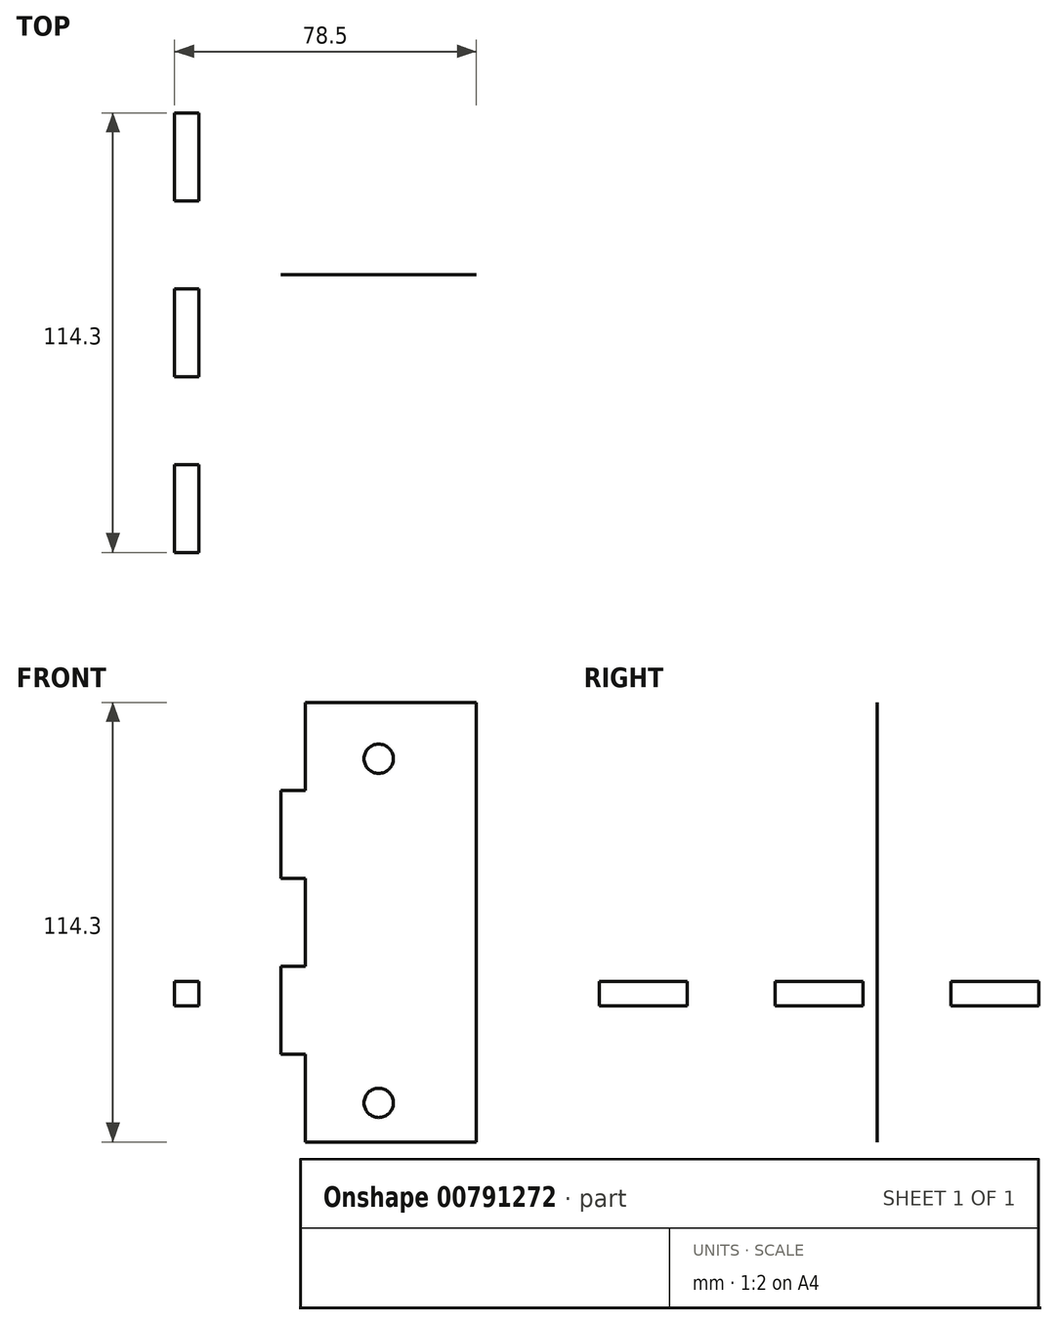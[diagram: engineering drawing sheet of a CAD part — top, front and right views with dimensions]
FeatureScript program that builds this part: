
annotation { "Feature Type Name" : "Feature", "Feature Type Description" : "" }
export const myFeature = defineFeature(function(context is Context, id is Id, definition is map)
    precondition{}
    {
        {
            var Q0;
            Q0=qCreatedBy(makeId("Top.planeOp"),FACE);
            var sketch = newSketch(context, id + "F0", { "sketchPlane" : qUnion([Q0])});
            skLineSegment(sketch, "E0.bottom", {"start": v(-68.61, 42.12) * mm, "end": v(-17.81, 42.12) * mm});
            skLineSegment(sketch, "E0.top", {"start": v(-68.61, -72.18) * mm, "end": v(-17.81, -72.18) * mm});
            skLineSegment(sketch, "E0.right", {"start": v(-17.81, 42.12) * mm, "end": v(-17.81, 19.26) * mm});
            skLineSegment(sketch, "E1", {"start": v(-17.81, -3.6) * mm, "end": v(-17.81, -26.46) * mm});
            skLineSegment(sketch, "E2", {"start": v(-17.81, -49.32) * mm, "end": v(-17.81, -72.18) * mm});
            skLineSegment(sketch, "E3", {"start": v(-17.81, -49.32) * mm, "end": v(-24.16, -49.32) * mm});
            skLineSegment(sketch, "E4", {"start": v(-24.16, -49.32) * mm, "end": v(-24.16, -26.46) * mm});
            skLineSegment(sketch, "E5", {"start": v(-24.16, -26.46) * mm, "end": v(-17.81, -26.46) * mm});
            skLineSegment(sketch, "E6", {"start": v(-17.81, -3.6) * mm, "end": v(-24.16, -3.6) * mm});
            skLineSegment(sketch, "E7", {"start": v(-24.16, -3.6) * mm, "end": v(-24.16, 19.26) * mm});
            skLineSegment(sketch, "E8", {"start": v(-24.16, 19.26) * mm, "end": v(-17.81, 19.26) * mm});
            skLineSegment(sketch, "E9.MirrorCS", {"start": v(-119.41, -49.32) * mm, "end": v(-113.06, -49.32) * mm});
            skLineSegment(sketch, "E10.MirrorCS", {"start": v(-113.06, 19.26) * mm, "end": v(-119.41, 19.26) * mm});
            skLineSegment(sketch, "E11.MirrorCS", {"start": v(-113.06, -26.46) * mm, "end": v(-119.41, -26.46) * mm});
            skLineSegment(sketch, "E12.MirrorCS", {"start": v(-119.41, -3.6) * mm, "end": v(-113.06, -3.6) * mm});
            skLineSegment(sketch, "E13.MirrorCS", {"start": v(-119.41, -49.32) * mm, "end": v(-119.41, -72.18) * mm});
            skLineSegment(sketch, "E14.MirrorCS", {"start": v(-119.41, -3.6) * mm, "end": v(-119.41, -26.46) * mm});
            skLineSegment(sketch, "E15.MirrorCS", {"start": v(-68.61, -72.18) * mm, "end": v(-119.41, -72.18) * mm});
            skLineSegment(sketch, "E16.MirrorCS", {"start": v(-113.06, -49.32) * mm, "end": v(-113.06, -26.46) * mm});
            skLineSegment(sketch, "E17.MirrorCS", {"start": v(-68.61, 42.12) * mm, "end": v(-119.41, 42.12) * mm});
            skLineSegment(sketch, "E18.MirrorCS", {"start": v(-113.06, -3.6) * mm, "end": v(-113.06, 19.26) * mm});
            skLineSegment(sketch, "E19.MirrorCS", {"start": v(-119.41, 42.12) * mm, "end": v(-119.41, 19.26) * mm});
            skLineSegment(sketch, "E20", {"start": v(-24.16, 19.26) * mm, "end": v(-24.16, 42.12) * mm});
            skLineSegment(sketch, "E21", {"start": v(-24.16, -49.32) * mm, "end": v(-24.16, -72.18) * mm});
            skLineSegment(sketch, "E22.bottom", {"start": v(-24.16, 42.12) * mm, "end": v(26.64, 42.12) * mm});
            skLineSegment(sketch, "E22.top", {"start": v(-24.16, -72.18) * mm, "end": v(26.64, -72.18) * mm});
            skLineSegment(sketch, "E22.left", {"start": v(-24.16, 42.12) * mm, "end": v(-24.16, -72.18) * mm});
            skLineSegment(sketch, "E22.right", {"start": v(26.64, 42.12) * mm, "end": v(26.64, -72.18) * mm});
            skSolve(sketch);
        }
        {
            var Q0;
            {var subQ0=sQuery(id+"F0.wireOp",EDGE,"E0.right");Q0=makeQuery(id+"F0.imprint","IMPRINT",FACE,{"disambiguationData":[TD([[makeQuery(id+"F0.imprint","IMPRINT",EDGE,{"derivedFrom":subQ0}),-1.0]])]});}
            var Q1;
            {var subQ0=sQuery(id+"F0.wireOp",EDGE,"E3");Q1=makeQuery(id+"F0.imprint","IMPRINT",FACE,{"disambiguationData":[TD([[makeQuery(id+"F0.imprint","IMPRINT",EDGE,{"derivedFrom":subQ0}),1.0]])]});}
            var Q2;
            {var subQ0=sQuery(id+"F0.wireOp",EDGE,"E0.bottom");Q2=makeQuery(id+"F0.imprint","IMPRINT",FACE,{"disambiguationData":[TD([[makeQuery(id+"F0.imprint","IMPRINT",EDGE,{"derivedFrom":subQ0}),-1.0]])]});}
            var Q3;
            {var subQ0=sQuery(id+"F0.wireOp",EDGE,"E5");Q3=makeQuery(id+"F0.imprint","IMPRINT",FACE,{"disambiguationData":[TD([[makeQuery(id+"F0.imprint","IMPRINT",EDGE,{"derivedFrom":subQ0}),1.0]])]});}
            extrude(context, id + "F1", {"entities" : qUnion([Q0, Q1, Q2, Q3]), "depth" : 6.35 * mm, "offsetDistance" : 25.4 * mm});
        }
        {
            var Q0;
            Q0=qCreatedBy(makeId("Front.planeOp"),FACE);
            var sketch = newSketch(context, id + "F2", { "sketchPlane" : qUnion([Q0])});
            skLineSegment(sketch, "E23.bottom", {"start": v(3.54, 78.96) * mm, "end": v(54.34, 78.96) * mm});
            skLineSegment(sketch, "E23.top", {"start": v(3.54, -35.34) * mm, "end": v(54.34, -35.34) * mm});
            skLineSegment(sketch, "E23.left", {"start": v(3.54, 78.96) * mm, "end": v(3.54, -35.34) * mm});
            skLineSegment(sketch, "E23.right", {"start": v(54.34, 78.96) * mm, "end": v(54.34, -35.34) * mm});
            skLineSegment(sketch, "E24", {"start": v(9.9, 78.96) * mm, "end": v(9.9, -35.34) * mm});
            skLineSegment(sketch, "E25", {"start": v(3.54, 56.1) * mm, "end": v(9.9, 56.1) * mm});
            skLineSegment(sketch, "E26", {"start": v(3.54, 33.24) * mm, "end": v(9.9, 33.24) * mm});
            skLineSegment(sketch, "E27", {"start": v(3.54, 10.38) * mm, "end": v(9.9, 10.38) * mm});
            skLineSegment(sketch, "E28", {"start": v(3.54, -12.48) * mm, "end": v(9.9, -12.48) * mm});
            skCircle(sketch, "E29", {"center": v(28.94, 64.31) * mm, "radius": 3.81 * mm});
            skCircle(sketch, "E30", {"center": v(28.94, -25.18) * mm, "radius": 3.81 * mm});
            skSolve(sketch);
        }
        {
            var Q0;
            {var subQ0=sQuery(id+"F2.wireOp",EDGE,"E25");Q0=makeQuery(id+"F2.imprint","IMPRINT",FACE,{"disambiguationData":[TD([[makeQuery(id+"F2.imprint","IMPRINT",EDGE,{"derivedFrom":subQ0}),-1.0]])]});}
            var Q1;
            {var subQ0=sQuery(id+"F2.wireOp",EDGE,"E27");Q1=makeQuery(id+"F2.imprint","IMPRINT",FACE,{"disambiguationData":[TD([[makeQuery(id+"F2.imprint","IMPRINT",EDGE,{"derivedFrom":subQ0}),-1.0]])]});}
            var Q2;
            {var subQ4=sQuery(id+"F2.wireOp",EDGE,"E23.right");Q2=makeQuery(id+"F2.imprint","IMPRINT",FACE,{"disambiguationData":[TD([[makeQuery(id+"F2.imprint","IMPRINT",EDGE,{"derivedFrom":subQ4}),-1.0]])]});}
            extrude(context, id + "F3", {"entities" : qUnion([Q0, Q1, Q2]), "depth" : 1 / 101.6 * mm, "offsetDistance" : 25.4 * mm});
        }
    });
